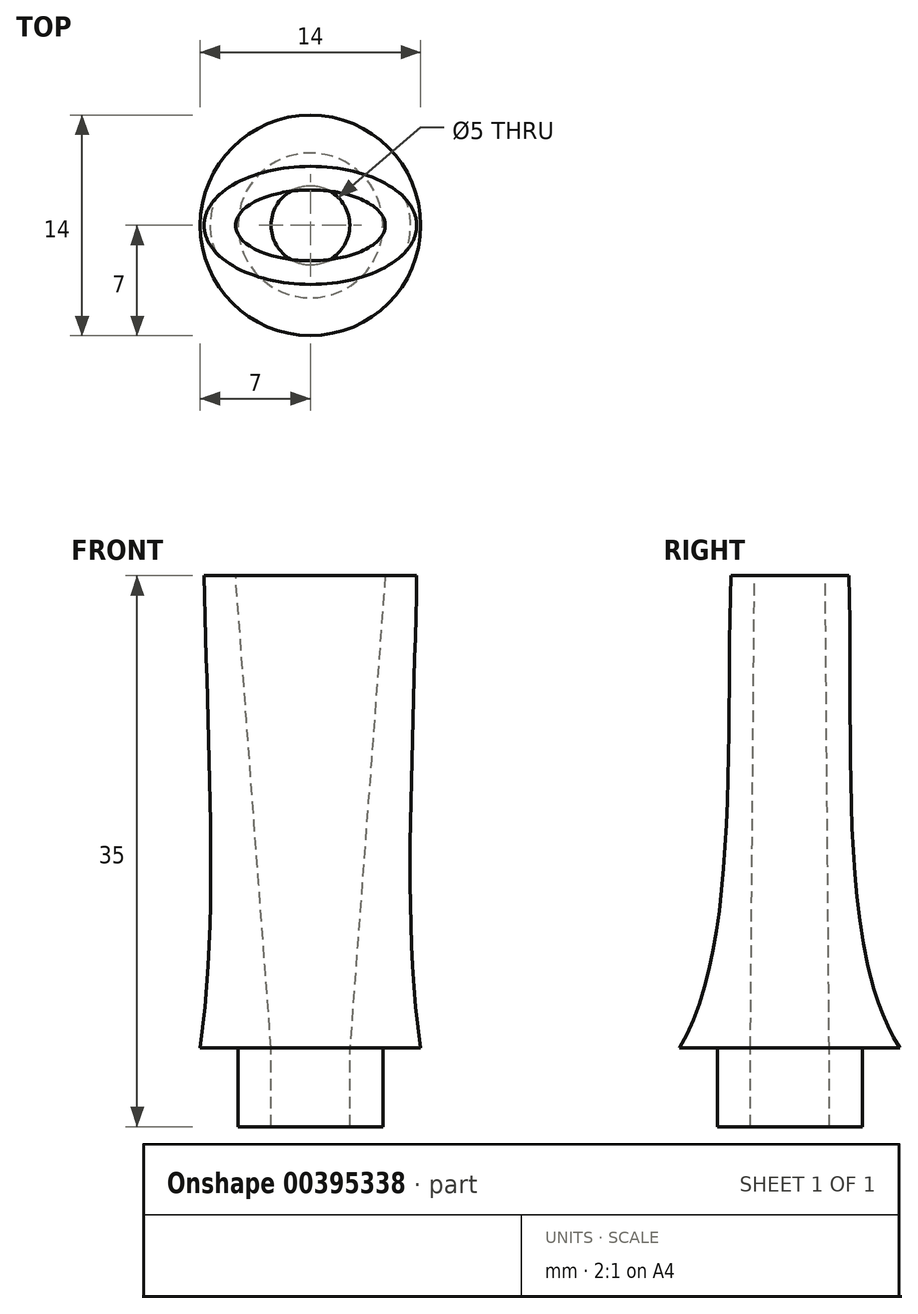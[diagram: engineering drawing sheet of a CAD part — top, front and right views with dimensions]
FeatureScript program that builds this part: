
annotation { "Feature Type Name" : "Feature", "Feature Type Description" : "" }
export const myFeature = defineFeature(function(context is Context, id is Id, definition is map)
    precondition{}
    {
        {
            var Q0;
            Q0=qCreatedBy(makeId("Top.planeOp"),FACE);
            var sketch = newSketch(context, id + "F0", { "sketchPlane" : qUnion([Q0])});
            skCircle(sketch, "E0", {"center": v(0, 0) * mm, "radius": 4.6 * mm});
            skSolve(sketch);
        }
        {
            var Q0;
            Q0 = qSketchRegion(id + "F0", true);
            extrude(context, id + "F1", {"entities" : qUnion([Q0]), "depth" : 5 * mm});
        }
        {
            var Q0;
            Q0=makeQuery(id+"F1.opExtrude","CAP_FACE",FACE,{"disambiguationData":[OSD([sQuery(id+"F0.wireOp",EDGE,"E0")])],"isStart":false});
            var sketch = newSketch(context, id + "F2", { "sketchPlane" : qUnion([Q0])});
            skArc(sketch, "E1", {"start": v(7, 0) * mm, "mid": v(4.95, 4.95) * mm, "end": v(0, 7) * mm});
            skArc(sketch, "E2", {"start": v(-7, 0) * mm, "mid": v(-4.95, -4.95) * mm, "end": v(0, -7) * mm});
            skArc(sketch, "E3", {"start": v(0, 7) * mm, "mid": v(-4.95, 4.95) * mm, "end": v(-7, 0) * mm});
            skArc(sketch, "E4", {"start": v(0, -7) * mm, "mid": v(4.95, -4.95) * mm, "end": v(7, 0) * mm});
            skSolve(sketch);
        }
        {
            var Q0;
            Q0=qCreatedBy(makeId("Top.planeOp"),FACE);
            cPlane(context, id + "F3", {"entities" : qUnion([Q0]), "cplaneType" : CPlaneType.OFFSET, "offset" : 35 * mm, "width" : 150 * mm, "height" : 150 * mm});
        }
        {
            var Q0;
            Q0=qCreatedBy(id+"F3.planeOp",FACE);
            var sketch = newSketch(context, id + "F4", { "sketchPlane" : qUnion([Q0])});
            skEllipticalArc(sketch, "E5", {});
            skEllipticalArc(sketch, "E6", {});
            skEllipticalArc(sketch, "E7", {});
            skEllipticalArc(sketch, "E8", {});
            const initialGuessF4  = {"E5": [0, 0, 1, 0, 0.00675, 0.00375, 1.5707963267948966, 3.141592653589793], "E6": [0, 0, 1, 0, 0.00675, 0.00375, 4.71238898038469, 0], "E7": [0, 0, 1, 0, 0.00675, 0.00375, 0, 1.5707963267948966], "E8": [0, 0, 1, 0, 0.00675, 0.00375, 3.141592653589793, 4.71238898038469]};
            skSetInitialGuess(sketch, initialGuessF4);
            skSolve(sketch);
        }
        {
            var Q0;
            Q0=makeQuery(id+"F2.imprint","IMPRINT",FACE,{"disambiguationData":[TD([[makeQuery(id+"F2.imprint","IMPRINT",EDGE,{"derivedFrom":makeQuery(id+"F1.opExtrude","CAP_EDGE",EDGE,{"disambiguationData":[OSD([sQuery(id+"F0.wireOp",EDGE,"E0")])],"isStart":false})}),1.0]])]});
            var sketch = newSketch(context, id + "F5", { "sketchPlane" : qUnion([Q0])});
            skCircle(sketch, "E9", {"center": v(0, 0) * mm, "radius": 2.5 * mm});
            skSolve(sketch);
        }
        {
            var Q0;
            Q0 = qSketchRegion(id + "F5", true);
            extrude(context, id + "F6", {"entities" : qUnion([Q0]), "operationType" : NewBodyOperationType.REMOVE, "oppositeDirection" : true, "depth" : 25 * mm});
        }
        {
            var Q0;
            Q0=qCreatedBy(makeId("Right.planeOp"),FACE);
            var sketch = newSketch(context, id + "F7", { "sketchPlane" : qUnion([Q0])});
            skFitSpline(sketch, "E10", {"points": [v(7, 5) * mm, v(3.75, 35) * mm], "startDerivative": vector(-12.24, 18.6) * mm, "endDerivative": vector(-1.02, 30.5) * mm});
            skFitSpline(sketch, "E11", {"points": [v(-7, 5) * mm, v(-3.75, 35) * mm], "startDerivative": vector(11.38, 18.74) * mm, "endDerivative": vector(0.92, 30.76) * mm});
            skSolve(sketch);
        }
        {
            var Q0;
            Q0=qCreatedBy(makeId("Front.planeOp"),FACE);
            var sketch = newSketch(context, id + "F8", { "sketchPlane" : qUnion([Q0])});
            skFitSpline(sketch, "E12", {"points": [v(-6.75, 35) * mm, v(-7, 5) * mm], "startDerivative": vector(0.82, -38) * mm, "endDerivative": vector(-3.45, -24.8) * mm});
            skFitSpline(sketch, "E13", {"points": [v(7, 5) * mm, v(6.75, 35) * mm], "startDerivative": vector(-3.54, 24.8) * mm, "endDerivative": vector(0.76, 38.78) * mm});
            skSolve(sketch);
        }
        {
            var Q1;
            Q1 = qSketchRegion(id + "F2", true);
            var Q2;
            Q2 = qSketchRegion(id + "F4", true);
            var Q3;
            Q3=sQuery(id+"F8.wireOp",EDGE,"E12");
            var Q4;
            Q4=sQuery(id+"F8.wireOp",EDGE,"E13");
            var Q5;
            Q5=sQuery(id+"F7.wireOp",EDGE,"E10");
            var Q6;
            Q6=sQuery(id+"F7.wireOp",EDGE,"E11");
            loft(context, id + "F9", {"operationType" : NewBodyOperationType.ADD, "addGuides" : true, "sheetProfilesArray" : [{ "sheetProfileEntities" : qUnion([Q1]) }, { "sheetProfileEntities" : qUnion([Q2]) }], "guidesArray" : [{ "guideEntities" : qUnion([Q3]), "guideDerivativeType" : LoftGuideDerivativeType.DEFAULT, "guideDerivativeMagnitude" : 1 }, { "guideEntities" : qUnion([Q4]), "guideDerivativeType" : LoftGuideDerivativeType.DEFAULT, "guideDerivativeMagnitude" : 1 }, { "guideEntities" : qUnion([Q5]), "guideDerivativeType" : LoftGuideDerivativeType.DEFAULT, "guideDerivativeMagnitude" : 1 }, { "guideEntities" : qUnion([Q6]), "guideDerivativeType" : LoftGuideDerivativeType.DEFAULT, "guideDerivativeMagnitude" : 1 }]});
        }
        {
            var Q0;
            Q0=makeQuery(id+"F9.opLoft","CAP_FACE",FACE,{"disambiguationData":[OSD([makeQuery(id+"F4.imprint","IMPRINT",FACE,{"disambiguationData":[TD([[makeQuery(id+"F4.imprint","IMPRINT",EDGE,{"derivedFrom":sQuery(id+"F4.wireOp",EDGE,"E5")}),1.0]])]})])],"isStart":true});
            var sketch = newSketch(context, id + "F10", { "sketchPlane" : qUnion([Q0])});
            skEllipse(sketch, "E14", {"center": v(0, 0) * mm, "majorRadius": 4.75 * mm, "minorRadius": 2.25 * mm, "majorAxis": v(1, 0)});
            skSolve(sketch);
        }
        {
            var Q0;
            {var subQ0=sQuery(id+"F0.wireOp",EDGE,"E0");Q0=makeQuery(id+"F9.boolean.opBoolean","SPLIT",FACE,{"disambiguationData":[TD([makeQuery(id+"F1.opExtrude","SWEPT_FACE",FACE,{"disambiguationData":[OSD([subQ0])]})])],"derivedFrom":makeQuery(id+"F9.opLoft","CAP_FACE",FACE,{"disambiguationData":[OSD([makeQuery(id+"F2.imprint","IMPRINT",FACE,{"disambiguationData":[TD([[makeQuery(id+"F2.imprint","IMPRINT",EDGE,{"derivedFrom":makeQuery(id+"F1.opExtrude","CAP_EDGE",EDGE,{"disambiguationData":[OSD([subQ0])],"isStart":false})}),1.0]])]})])],"isStart":true})});}
            var sketch = newSketch(context, id + "F11", { "sketchPlane" : qUnion([Q0])});
            skCircle(sketch, "E15", {"center": v(0, 0) * mm, "radius": 2.5 * mm});
            skSolve(sketch);
        }
        {
            var Q1;
            Q1 = qSketchRegion(id + "F10", true);
            var Q2;
            Q2 = qSketchRegion(id + "F11", true);
            loft(context, id + "F12", {"operationType" : NewBodyOperationType.REMOVE, "sheetProfilesArray" : [{ "sheetProfileEntities" : qUnion([Q1]) }, { "sheetProfileEntities" : qUnion([Q2]) }]});
        }
    });
